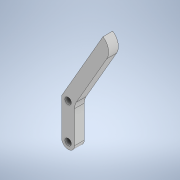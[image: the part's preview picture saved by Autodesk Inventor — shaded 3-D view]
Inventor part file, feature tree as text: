
AUTODESK INVENTOR PART (.ipt)
format: ipt  version: 2021 (Build 250183000, 183)  size: 126,464 bytes
history: native  units: mm
features: extrude x1, fillet x1, sketch x1
ambient origin geometry x8: Origin, YZ Plane, XZ Plane, XY Plane, X Axis, Y Axis, Z Axis, Center Point
bodies: Solid1 (feature_tree)
feature tree (3):
  extrude  "Extrusion1"  Depth=8.0mm
  fillet  "Fillet1"  Radius=22.0mm
  sketch  "Sketch1"  dims[d0=4.0mm d1=8.0mm d2=22.0mm d3=4.0mm d4=8.0mm d5=50.0mm d6=150.0deg d7=4.0mm d8=8.0mm d9=6.0mm d10=0.0mm d11=8.0mm d13=8.0mm]
